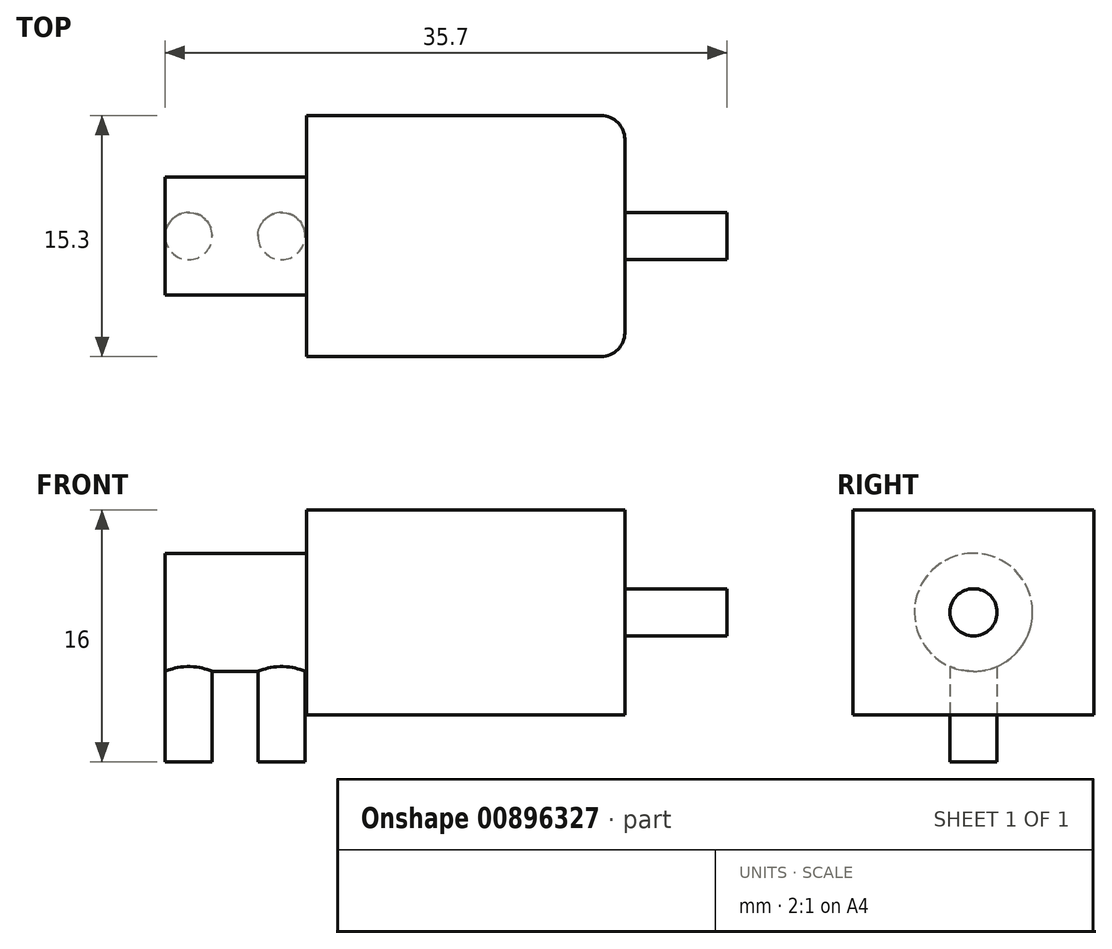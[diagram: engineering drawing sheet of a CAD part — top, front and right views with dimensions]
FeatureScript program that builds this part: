
annotation { "Feature Type Name" : "Feature", "Feature Type Description" : "" }
export const myFeature = defineFeature(function(context is Context, id is Id, definition is map)
    precondition{}
    {
        {
            var Q0;
            Q0=qCreatedBy(makeId("Top.planeOp"),FACE);
            var sketch = newSketch(context, id + "F0", { "sketchPlane" : qUnion([Q0])});
            skLineSegment(sketch, "E0.bottom", {"start": v(-10.1, 7.65) * mm, "end": v(10.1, 7.65) * mm});
            skLineSegment(sketch, "E0.top", {"start": v(-10.1, -7.65) * mm, "end": v(10.1, -7.65) * mm});
            skLineSegment(sketch, "E0.left", {"start": v(-10.1, 7.65) * mm, "end": v(-10.1, -7.65) * mm});
            skLineSegment(sketch, "E0.right", {"start": v(10.1, 7.65) * mm, "end": v(10.1, -7.65) * mm});
            skSolve(sketch);
        }
        {
            var Q0;
            Q0 = qSketchRegion(id + "F0", true);
            extrude(context, id + "F1", {"entities" : qUnion([Q0]), "depth" : 13 * mm, "offsetDistance" : 25 * mm});
        }
        {
            var Q0;
            Q0=makeQuery(id+"F1.opExtrude","SWEPT_EDGE",EDGE,{"disambiguationData":[OSD([sQuery(id+"F0.wireOp",EDGE,"E0.top"),sQuery(id+"F0.wireOp",EDGE,"E0.right")])]});
            var Q1;
            Q1=makeQuery(id+"F1.opExtrude","SWEPT_EDGE",EDGE,{"disambiguationData":[OSD([sQuery(id+"F0.wireOp",EDGE,"E0.bottom"),sQuery(id+"F0.wireOp",EDGE,"E0.right")])]});
            fillet(context, id + "F2", {"entities" : qUnion([Q0, Q1]), "radius" : 1.5 * mm, "tangentPropagation" : true, "allowEdgeOverflow" : false});
        }
        {
            var Q0;
            Q0=makeQuery(id+"F1.opExtrude","SWEPT_FACE",FACE,{"disambiguationData":[OSD([sQuery(id+"F0.wireOp",EDGE,"E0.left")])]});
            var sketch = newSketch(context, id + "F3", { "sketchPlane" : qUnion([Q0])});
            skCircle(sketch, "E1", {"center": v(0, 6.5) * mm, "radius": 3.75 * mm});
            skSolve(sketch);
        }
        {
            var Q0;
            Q0 = qSketchRegion(id + "F3", true);
            extrude(context, id + "F4", {"entities" : qUnion([Q0]), "operationType" : NewBodyOperationType.ADD, "depth" : 9 * mm, "offsetDistance" : 25 * mm});
        }
        {
            var Q0;
            Q0=makeQuery(id+"F1.opExtrude","SWEPT_FACE",FACE,{"disambiguationData":[OSD([sQuery(id+"F0.wireOp",EDGE,"E0.right")])]});
            var sketch = newSketch(context, id + "F5", { "sketchPlane" : qUnion([Q0])});
            skCircle(sketch, "E2", {"center": v(0, 6.5) * mm, "radius": 1.5 * mm});
            skSolve(sketch);
        }
        {
            var Q0;
            Q0 = qSketchRegion(id + "F5", true);
            extrude(context, id + "F6", {"entities" : qUnion([Q0]), "operationType" : NewBodyOperationType.ADD, "depth" : 6.5 * mm, "offsetDistance" : 25 * mm});
        }
        {
            var Q0;
            Q0=qCreatedBy(makeId("Top.planeOp"),FACE);
            var sketch = newSketch(context, id + "F7", { "sketchPlane" : qUnion([Q0])});
            skCircle(sketch, "E3", {"center": v(-17.6, 0) * mm, "radius": 1.5 * mm});
            skCircle(sketch, "E4", {"center": v(-11.7, 0) * mm, "radius": 1.5 * mm});
            skSolve(sketch);
        }
        {
            var Q0;
            Q0 = qSketchRegion(id + "F7", true);
            extrude(context, id + "F8", {"entities" : qUnion([Q0]), "operationType" : NewBodyOperationType.ADD, "depth" : 5 * mm, "offsetDistance" : 25 * mm, "hasSecondDirection" : true, "secondDirectionOppositeDirection" : true, "secondDirectionDepth" : 3 * mm});
        }
    });
